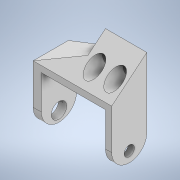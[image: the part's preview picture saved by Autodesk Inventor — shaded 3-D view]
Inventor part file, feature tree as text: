
AUTODESK INVENTOR PART (.ipt)
format: ipt  version: 2022.1 (Build 261234000, 234)  size: 210,432 bytes
history: native  units: mm
features: extrude x10, sketch x10, fillet x1
ambient origin geometry x8: Origin, YZ Plane, XZ Plane, XY Plane, X Axis, Y Axis, Z Axis, Center Point
bodies: Solid1 (feature_tree)
feature tree (21):
  extrude  "Extrusion1"  Depth=4.0mm
  extrude  "Extrusion2"  Depth=3.0mm
  extrude  "Extrusion3"  Depth=17.0mm
  extrude  "Extrusion4"  Depth=14.0mm
  extrude  "Extrusion5"  Depth=17.0mm
  extrude  "Extrusion6"  Depth=10.0mm TaperAngle=0.0deg
  extrude  "Extrusion7"  Depth=17.0mm
  extrude  "Extrusion8"  Depth=7.0mm
  extrude  "Extrusion9"  Depth=8.5mm
  fillet  "Fillet1"  Radius=8.5mm
  extrude  "Extrusion10"  Depth=14.0mm TaperAngle=0.0deg
  sketch  "Sketch1"  dims[d0=4.0mm d1=25.0mm]
  sketch  "Sketch2"  dims[d2=3.0mm d3=25.0mm]
  sketch  "Sketch3"  dims[d4=31.0mm d6=17.0mm]
  sketch  "Sketch4"  dims[d7=17.0mm d8=0.0mm d9=14.0mm]
  sketch  "Sketch5"  dims[d10=17.0mm d11=0.0mm d12=15.0mm]
  sketch  "Sketch6"  dims[d13=13.0mm d14=10.0mm d15=0.0mm]
  sketch  "Sketch7"  dims[d16=20.0mm d17=17.0mm]
  sketch  "Sketch8"  dims[d18=7.0mm d19=7.0mm]
  sketch  "Sketch9"  dims[d20=8.5mm d21=5.0mm d22=8.5mm]
  sketch  "Sketch10"  dims[d23=5.0mm d24=14.0mm d25=0.0mm d26=3.0mm d27=3.0mm d28=14.0mm d29=0.0mm d30=10.0mm d31=0.0mm d32=18.0mm d33=7.0mm d34=7.0mm d35=10.0mm d36=0.0mm d37=7.5mm d38=5.0mm d39=8.5mm d40=10.0mm d41=0.0mm d42=5.0mm d43=5.0mm d44=8.5mm d45=10.0mm d46=0.0mm d47=8.5mm d48=0.0mm d49=4.0mm d50=15.0mm d51=0.0mm d52=2.0mm d53=0.0mm]
